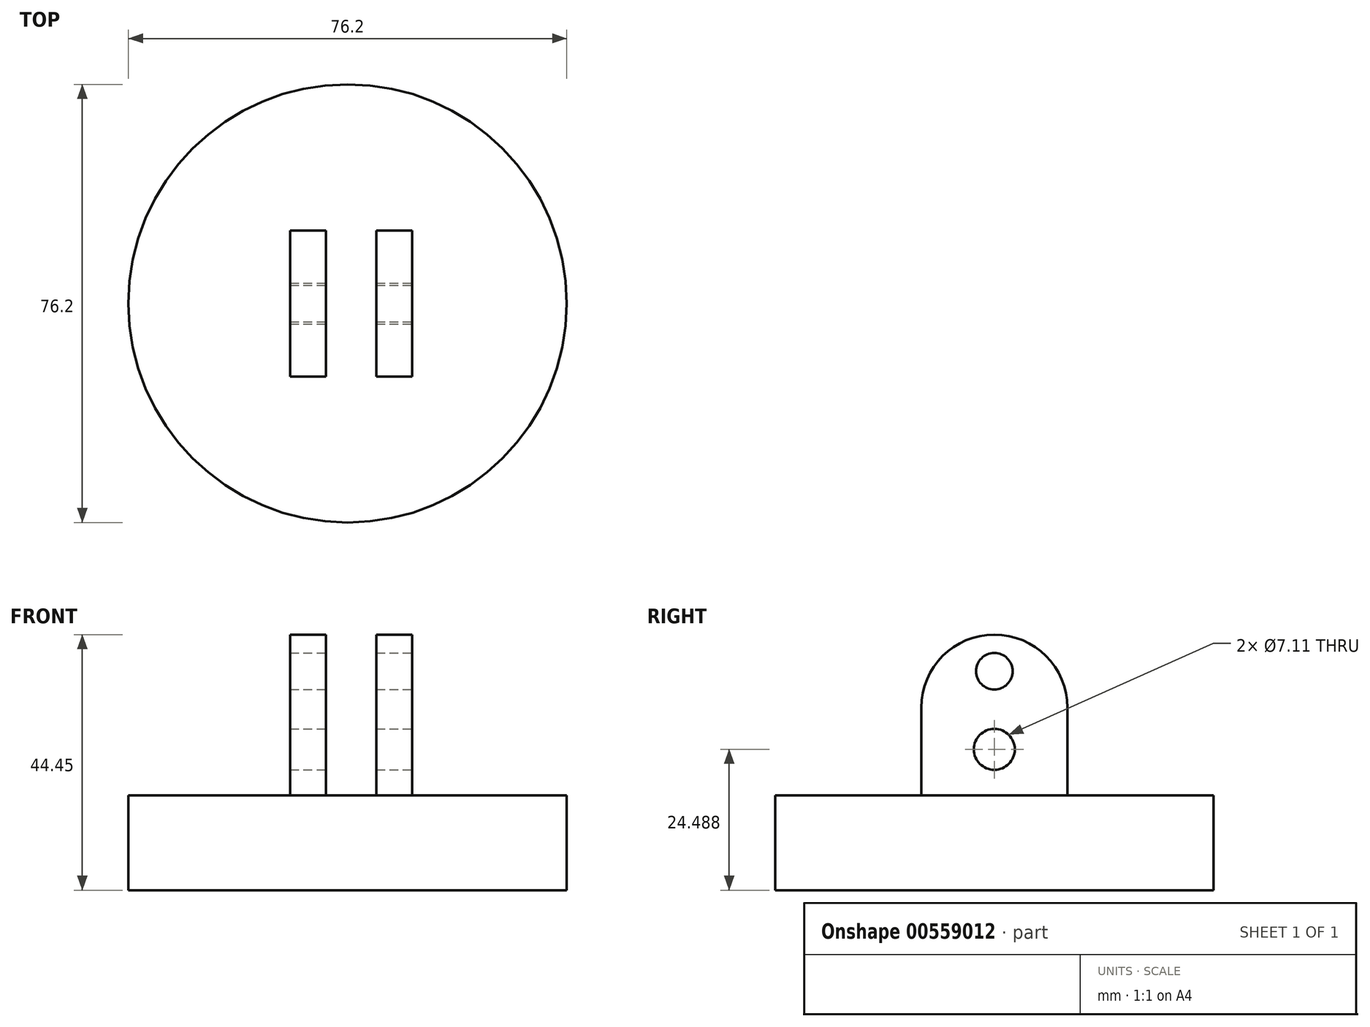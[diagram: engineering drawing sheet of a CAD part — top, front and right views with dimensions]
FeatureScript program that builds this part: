
annotation { "Feature Type Name" : "Feature", "Feature Type Description" : "" }
export const myFeature = defineFeature(function(context is Context, id is Id, definition is map)
    precondition{}
    {
        {
            var Q0;
            Q0=qCreatedBy(makeId("Top.planeOp"),FACE);
            var sketch = newSketch(context, id + "F0", { "sketchPlane" : qUnion([Q0])});
            skCircle(sketch, "E0", {"center": v(0, 0) * mm, "radius": 38.1 * mm});
            skSolve(sketch);
        }
        {
            var Q0;
            Q0=makeQuery(id+"F0.imprint","IMPRINT",FACE,{"disambiguationData":[TD([[makeQuery(id+"F0.imprint","IMPRINT",EDGE,{"derivedFrom":sQuery(id+"F0.wireOp",EDGE,"E0")}),1.0]])]});
            extrude(context, id + "F1", {"entities" : qUnion([Q0]), "depth" : 16.5 * mm, "offsetDistance" : 25.4 * mm});
        }
        {
            var Q0;
            Q0=makeQuery(id+"F1.opExtrude","CAP_FACE",FACE,{"disambiguationData":[OSD([sQuery(id+"F0.wireOp",EDGE,"E0")])],"isStart":false});
            var sketch = newSketch(context, id + "F2", { "sketchPlane" : qUnion([Q0])});
            skLineSegment(sketch, "E1.bottom", {"start": v(-9.96, 12.7) * mm, "end": v(-3.75, 12.7) * mm});
            skLineSegment(sketch, "E1.top", {"start": v(-9.96, -12.7) * mm, "end": v(-3.75, -12.7) * mm});
            skLineSegment(sketch, "E1.left", {"start": v(-9.96, 12.7) * mm, "end": v(-9.96, -12.7) * mm});
            skLineSegment(sketch, "E1.right", {"start": v(-3.75, 12.7) * mm, "end": v(-3.75, -12.7) * mm});
            skPoint(sketch, "E1.middle", {"position": v(-6.86, 0) * mm});
            skLineSegment(sketch, "E2.bottom", {"start": v(11.22, 12.7) * mm, "end": v(5, 12.7) * mm});
            skLineSegment(sketch, "E2.top", {"start": v(11.22, -12.7) * mm, "end": v(5, -12.7) * mm});
            skLineSegment(sketch, "E2.left", {"start": v(11.22, 12.7) * mm, "end": v(11.22, -12.7) * mm});
            skLineSegment(sketch, "E2.right", {"start": v(5, 12.7) * mm, "end": v(5, -12.7) * mm});
            skPoint(sketch, "E2.middle", {"position": v(8.11, 0) * mm});
            skSolve(sketch);
        }
        {
            var Q0;
            Q0=makeQuery(id+"F2.imprint","IMPRINT",FACE,{"disambiguationData":[TD([[makeQuery(id+"F2.imprint","IMPRINT",EDGE,{"derivedFrom":sQuery(id+"F2.wireOp",EDGE,"E1.bottom")}),-1.0]])]});
            var Q1;
            Q1=makeQuery(id+"F2.imprint","IMPRINT",FACE,{"disambiguationData":[TD([[makeQuery(id+"F2.imprint","IMPRINT",EDGE,{"derivedFrom":sQuery(id+"F2.wireOp",EDGE,"E2.bottom")}),1.0]])]});
            extrude(context, id + "F3", {"entities" : qUnion([Q0, Q1]), "operationType" : NewBodyOperationType.ADD, "depth" : 27.94 * mm, "offsetDistance" : 25.4 * mm});
        }
        {
            var Q0;
            Q0=makeQuery(id+"F3.opExtrude","CAP_EDGE",EDGE,{"disambiguationData":[OSD([sQuery(id+"F2.wireOp",EDGE,"E1.bottom")])],"isStart":false});
            var Q1;
            Q1=makeQuery(id+"F3.opExtrude","CAP_EDGE",EDGE,{"disambiguationData":[OSD([sQuery(id+"F2.wireOp",EDGE,"E1.top")])],"isStart":false});
            var Q2;
            Q2=makeQuery(id+"F3.opExtrude","CAP_EDGE",EDGE,{"disambiguationData":[OSD([sQuery(id+"F2.wireOp",EDGE,"E2.top")])],"isStart":false});
            var Q3;
            Q3=makeQuery(id+"F3.opExtrude","CAP_EDGE",EDGE,{"disambiguationData":[OSD([sQuery(id+"F2.wireOp",EDGE,"E2.bottom")])],"isStart":false});
            fillet(context, id + "F4", {"entities" : qUnion([Q0, Q1, Q2, Q3]), "radius" : 12.7 * mm, "tangentPropagation" : true, "allowEdgeOverflow" : false});
        }
        {
            var Q0;
            Q0=makeQuery(id+"F3.opExtrude","SWEPT_FACE",FACE,{"disambiguationData":[OSD([sQuery(id+"F2.wireOp",EDGE,"E2.left")])]});
            var sketch = newSketch(context, id + "F5", { "sketchPlane" : qUnion([Q0])});
            skCircle(sketch, "E3", {"center": v(0, 24.49) * mm, "radius": 3.56 * mm});
            skCircle(sketch, "E4", {"center": v(0, 38.08) * mm, "radius": 3.18 * mm});
            skSolve(sketch);
        }
        {
            var Q0;
            Q0=makeQuery(id+"F5.imprint","IMPRINT",FACE,{"disambiguationData":[TD([[makeQuery(id+"F5.imprint","IMPRINT",EDGE,{"derivedFrom":sQuery(id+"F5.wireOp",EDGE,"E3")}),1.0]])]});
            var Q1;
            Q1=makeQuery(id+"F5.imprint","IMPRINT",FACE,{"disambiguationData":[TD([[makeQuery(id+"F5.imprint","IMPRINT",EDGE,{"derivedFrom":sQuery(id+"F5.wireOp",EDGE,"E4")}),1.0]])]});
            extrude(context, id + "F6", {"entities" : qUnion([Q0, Q1]), "operationType" : NewBodyOperationType.REMOVE, "endBound" : BoundingType.THROUGH_ALL, "oppositeDirection" : true, "depth" : 25.4 * mm, "offsetDistance" : 25.4 * mm});
        }
    });
